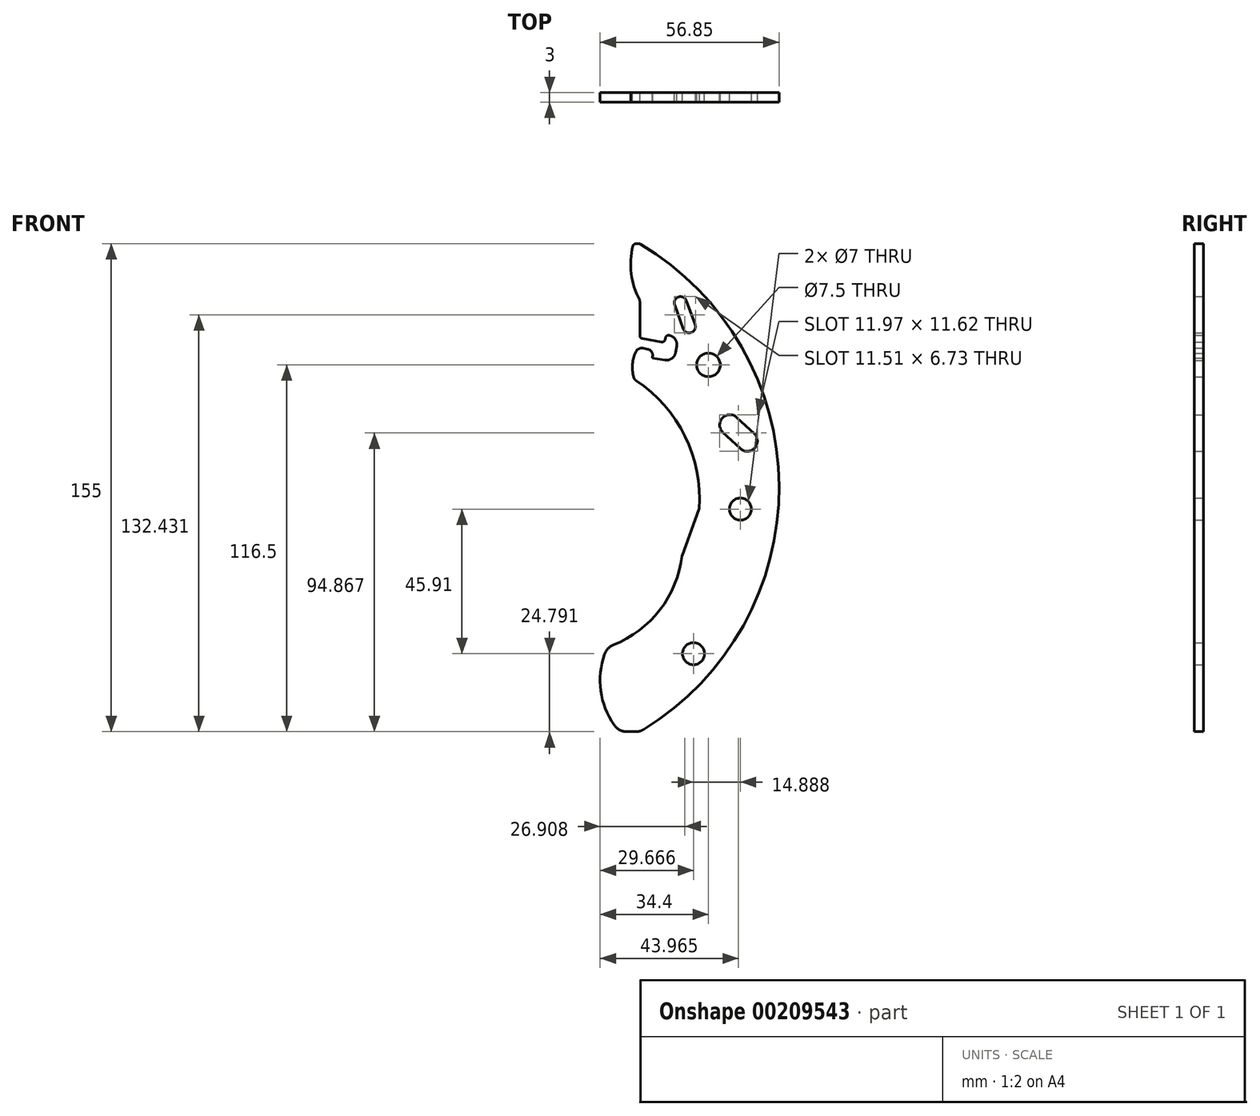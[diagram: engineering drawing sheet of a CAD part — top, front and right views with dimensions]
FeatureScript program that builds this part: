
annotation { "Feature Type Name" : "Feature", "Feature Type Description" : "" }
export const myFeature = defineFeature(function(context is Context, id is Id, definition is map)
    precondition{}
    {
        {
            var Q0;
            Q0=qCreatedBy(makeId("Front.planeOp"),FACE);
            var sketch = newSketch(context, id + "F0", { "sketchPlane" : qUnion([Q0])});
            skArc(sketch, "E0", {"start": v(46.98, -76.76) * mm, "mid": v(90, 0.58) * mm, "end": v(46, 77.36) * mm});
            skLineSegment(sketch, "E1", {"start": v(45.76, 77.5) * mm, "end": v(45.76, -77.5) * mm, "construction": true});
            skLineSegment(sketch, "E2", {"start": v(0, 0) * mm, "end": v(45.76, 0) * mm, "construction": true});
            skLineSegment(sketch, "E3", {"start": v(0, 0) * mm, "end": v(62.82, -52.7) * mm, "construction": true});
            skLineSegment(sketch, "E4", {"start": v(0, 0) * mm, "end": v(77.7, -6.8) * mm, "construction": true});
            skLineSegment(sketch, "E5", {"start": v(0, 0) * mm, "end": v(74.38, 19.93) * mm, "construction": true});
            skLineSegment(sketch, "E6", {"start": v(0, 0) * mm, "end": v(67.55, 39) * mm, "construction": true});
            skLineSegment(sketch, "E7", {"start": v(0, 0) * mm, "end": v(58.69, 58.69) * mm, "construction": true});
            skPoint(sketch, "E8", {"position": v(58.69, 58.69) * mm});
            skPoint(sketch, "E9", {"position": v(67.55, 39) * mm});
            skPoint(sketch, "E10", {"position": v(74.38, 19.93) * mm});
            skPoint(sketch, "E11", {"position": v(77.7, -6.8) * mm});
            skPoint(sketch, "E12", {"position": v(62.82, -52.7) * mm});
            skArc(sketch, "E13", {"start": v(60.57, 59.37) * mm, "mid": v(58, 60.57) * mm, "end": v(56.81, 58) * mm});
            skLineSegment(sketch, "E14", {"start": v(58.69, 58.69) * mm, "end": v(58.69, 50.69) * mm, "construction": true});
            skLineSegment(sketch, "E15", {"start": v(58.69, 58.69) * mm, "end": v(61.43, 51.17) * mm, "construction": true});
            skArc(sketch, "E16", {"start": v(59.55, 50.49) * mm, "mid": v(62.11, 49.3) * mm, "end": v(63.3, 51.86) * mm});
            skLineSegment(sketch, "E17", {"start": v(60.57, 59.37) * mm, "end": v(63.3, 51.86) * mm});
            skLineSegment(sketch, "E18", {"start": v(56.81, 58) * mm, "end": v(59.55, 50.49) * mm});
            skLineSegment(sketch, "E19", {"start": v(0, 0) * mm, "end": v(0, 89.5) * mm, "construction": true});
            skLineSegment(sketch, "E20", {"start": v(0, 89.5) * mm, "end": v(74.38, 19.93) * mm, "construction": true});
            skLineSegment(sketch, "E21", {"start": v(74.38, 19.93) * mm, "end": v(79.85, 14.8) * mm, "construction": true});
            skArc(sketch, "E22", {"start": v(76.6, 22.3) * mm, "mid": v(72, 22.15) * mm, "end": v(72.16, 17.56) * mm});
            skArc(sketch, "E23", {"start": v(77.63, 12.43) * mm, "mid": v(82.23, 12.59) * mm, "end": v(82.07, 17.18) * mm});
            skLineSegment(sketch, "E24", {"start": v(76.6, 22.3) * mm, "end": v(82.07, 17.18) * mm});
            skLineSegment(sketch, "E25", {"start": v(77.63, 12.43) * mm, "end": v(72.16, 17.56) * mm});
            skLineSegment(sketch, "E26", {"start": v(0, 0) * mm, "end": v(24.42, -17.42) * mm, "construction": true});
            skArc(sketch, "E27", {"start": v(37.4, -49.93) * mm, "mid": v(52.16, -38.77) * mm, "end": v(59.17, -21.65) * mm});
            skLineSegment(sketch, "E28", {"start": v(0, 0) * mm, "end": v(59.18, -21.54) * mm, "construction": true});
            skLineSegment(sketch, "E29", {"start": v(0, 0) * mm, "end": v(35.46, -50.64) * mm, "construction": true});
            skLineSegment(sketch, "E30", {"start": v(0, 0) * mm, "end": v(19.7, -3.47) * mm, "construction": true});
            skArc(sketch, "E31", {"start": v(45.76, -40.16) * mm, "mid": v(46.32, -39.75) * mm, "end": v(46.88, -39.34) * mm, "construction": true});
            skLineSegment(sketch, "E32", {"start": v(0, 0) * mm, "end": v(44.02, 34.39) * mm, "construction": true});
            skLineSegment(sketch, "E33", {"start": v(0, 0) * mm, "end": v(64.57, -6.79) * mm, "construction": true});
            skArc(sketch, "E34.trimOffspring", {"start": v(64.58, -6.65) * mm, "mid": v(60.09, 16.37) * mm, "end": v(44.62, 34) * mm});
            skLineSegment(sketch, "E35", {"start": v(64.53, -6.92) * mm, "end": v(59.22, -21.43) * mm});
            skLineSegment(sketch, "E36", {"start": v(44.37, -77.5) * mm, "end": v(41.7, -77.5) * mm});
            skArc(sketch, "E37", {"start": v(34.53, -52.93) * mm, "mid": v(33.38, -64.5) * mm, "end": v(37.59, -75.34) * mm});
            skPoint(sketch, "E38.visualSharp", {"position": v(35.46, -50.64) * mm});
            skArc(sketch, "E38.filletArc", {"start": v(37.4, -49.93) * mm, "mid": v(35.64, -51.12) * mm, "end": v(34.53, -52.93) * mm});
            skPoint(sketch, "E39.visualSharp", {"position": v(39.26, -77.5) * mm});
            skArc(sketch, "E39.filletArc", {"start": v(37.59, -75.34) * mm, "mid": v(39.38, -76.93) * mm, "end": v(41.7, -77.5) * mm});
            skPoint(sketch, "E40.visualSharp", {"position": v(45.76, -77.5) * mm});
            skArc(sketch, "E40.filletArc", {"start": v(44.37, -77.5) * mm, "mid": v(45.73, -77.31) * mm, "end": v(46.98, -76.76) * mm});
            skLineSegment(sketch, "E41", {"start": v(45.48, 77.5) * mm, "end": v(44.53, 77.5) * mm});
            skPoint(sketch, "E42", {"position": v(45.76, 59.5) * mm});
            skArc(sketch, "E43", {"start": v(43.56, 76.74) * mm, "mid": v(43.03, 68.04) * mm, "end": v(45.64, 59.72) * mm});
            skLineSegment(sketch, "E44", {"start": v(45.76, 59.25) * mm, "end": v(45.76, 48.34) * mm});
            skLineSegment(sketch, "E45", {"start": v(46.58, 47.35) * mm, "end": v(52.65, 46.28) * mm});
            skLineSegment(sketch, "E46", {"start": v(53.8, 47.1) * mm, "end": v(53.9, 47.59) * mm});
            skLineSegment(sketch, "E47", {"start": v(55.05, 48.4) * mm, "end": v(55.05, 48.4) * mm});
            skLineSegment(sketch, "E48", {"start": v(57.49, 44.92) * mm, "end": v(57.14, 42.95) * mm});
            skLineSegment(sketch, "E49", {"start": v(53.67, 40.52) * mm, "end": v(49.73, 41.22) * mm});
            skLineSegment(sketch, "E50", {"start": v(49.73, 41.22) * mm, "end": v(49.81, 41.7) * mm});
            skLineSegment(sketch, "E51", {"start": v(48.2, 44.02) * mm, "end": v(46.65, 44.3) * mm});
            skArc(sketch, "E52", {"start": v(44.49, 43.16) * mm, "mid": v(43.45, 39.22) * mm, "end": v(43.79, 35.16) * mm});
            skPoint(sketch, "E53.visualSharp", {"position": v(56.62, 40) * mm});
            skArc(sketch, "E53.filletArc", {"start": v(53.67, 40.52) * mm, "mid": v(55.9, 41.02) * mm, "end": v(57.14, 42.95) * mm});
            skPoint(sketch, "E54.visualSharp", {"position": v(58, 47.88) * mm});
            skArc(sketch, "E54.filletArc", {"start": v(57.49, 44.92) * mm, "mid": v(57, 47.17) * mm, "end": v(55.05, 48.4) * mm});
            skPoint(sketch, "E55.visualSharp", {"position": v(53.64, 46.11) * mm});
            skArc(sketch, "E55.filletArc", {"start": v(52.65, 46.28) * mm, "mid": v(53.4, 46.45) * mm, "end": v(53.8, 47.1) * mm});
            skPoint(sketch, "E56.visualSharp", {"position": v(54.07, 48.57) * mm});
            skArc(sketch, "E56.filletArc", {"start": v(55.05, 48.4) * mm, "mid": v(54.3, 48.23) * mm, "end": v(53.9, 47.59) * mm});
            skPoint(sketch, "E57.visualSharp", {"position": v(50.16, 43.68) * mm});
            skArc(sketch, "E57.filletArc", {"start": v(49.81, 41.7) * mm, "mid": v(49.48, 43.2) * mm, "end": v(48.2, 44.02) * mm});
            skPoint(sketch, "E58.visualSharp", {"position": v(45.24, 44.55) * mm});
            skArc(sketch, "E58.filletArc", {"start": v(46.65, 44.3) * mm, "mid": v(45.38, 44.1) * mm, "end": v(44.49, 43.16) * mm});
            skPoint(sketch, "E59.visualSharp", {"position": v(44.02, 34.39) * mm});
            skArc(sketch, "E59.filletArc", {"start": v(43.79, 35.16) * mm, "mid": v(44.1, 34.5) * mm, "end": v(44.62, 34) * mm});
            skPoint(sketch, "E60.visualSharp", {"position": v(45.76, 47.5) * mm});
            skArc(sketch, "E60.filletArc", {"start": v(45.76, 48.34) * mm, "mid": v(46, 47.7) * mm, "end": v(46.58, 47.35) * mm});
            skPoint(sketch, "E61.visualSharp", {"position": v(45.76, 77.5) * mm});
            skArc(sketch, "E61.filletArc", {"start": v(46, 77.36) * mm, "mid": v(45.75, 77.46) * mm, "end": v(45.48, 77.5) * mm});
            skPoint(sketch, "E62.visualSharp", {"position": v(43.76, 77.5) * mm});
            skArc(sketch, "E62.filletArc", {"start": v(44.53, 77.5) * mm, "mid": v(43.91, 77.29) * mm, "end": v(43.56, 76.74) * mm});
            skArc(sketch, "E63.filletArc", {"start": v(45.76, 59.25) * mm, "mid": v(45.73, 59.49) * mm, "end": v(45.64, 59.72) * mm});
            skPoint(sketch, "E64.visualSharp", {"position": v(59.18, -21.54) * mm});
            skArc(sketch, "E64.filletArc", {"start": v(59.22, -21.43) * mm, "mid": v(59.19, -21.54) * mm, "end": v(59.17, -21.65) * mm});
            skPoint(sketch, "E65.visualSharp", {"position": v(64.57, -6.79) * mm});
            skArc(sketch, "E65.filletArc", {"start": v(64.53, -6.92) * mm, "mid": v(64.56, -6.78) * mm, "end": v(64.58, -6.65) * mm});
            skSolve(sketch);
        }
        {
            var Q0;
            Q0 = qSketchRegion(id + "F0", true);
            extrude(context, id + "F1", {"entities" : qUnion([Q0]), "depth" : 3 * mm});
        }
        {
            var Q0;
            Q0=sQuery(id+"F0.wireOp",VERTEX,"E9");
            var Q1;
            Q1=makeQuery(id+"F1.opExtrude","SWEPT_BODY",BODY,{"disambiguationData":[OSD([sQuery(id+"F0.wireOp",EDGE,"E0"),sQuery(id+"F0.wireOp",EDGE,"E13"),sQuery(id+"F0.wireOp",EDGE,"E16"),sQuery(id+"F0.wireOp",EDGE,"E17"),sQuery(id+"F0.wireOp",EDGE,"E18"),sQuery(id+"F0.wireOp",EDGE,"E22"),sQuery(id+"F0.wireOp",EDGE,"E23"),sQuery(id+"F0.wireOp",EDGE,"E24"),sQuery(id+"F0.wireOp",EDGE,"E25"),sQuery(id+"F0.wireOp",EDGE,"E27"),sQuery(id+"F0.wireOp",EDGE,"E34.trimOffspring"),sQuery(id+"F0.wireOp",EDGE,"E35"),sQuery(id+"F0.wireOp",EDGE,"E36"),sQuery(id+"F0.wireOp",EDGE,"E37"),sQuery(id+"F0.wireOp",EDGE,"E38.filletArc"),sQuery(id+"F0.wireOp",EDGE,"E39.filletArc"),sQuery(id+"F0.wireOp",EDGE,"E40.filletArc"),sQuery(id+"F0.wireOp",EDGE,"E41"),sQuery(id+"F0.wireOp",EDGE,"E43"),sQuery(id+"F0.wireOp",EDGE,"E44"),sQuery(id+"F0.wireOp",EDGE,"E45"),sQuery(id+"F0.wireOp",EDGE,"E46"),sQuery(id+"F0.wireOp",EDGE,"E48"),sQuery(id+"F0.wireOp",EDGE,"E49"),sQuery(id+"F0.wireOp",EDGE,"E50"),sQuery(id+"F0.wireOp",EDGE,"E51"),sQuery(id+"F0.wireOp",EDGE,"E52"),sQuery(id+"F0.wireOp",EDGE,"E53.filletArc"),sQuery(id+"F0.wireOp",EDGE,"E54.filletArc"),sQuery(id+"F0.wireOp",EDGE,"E55.filletArc"),sQuery(id+"F0.wireOp",EDGE,"E56.filletArc"),sQuery(id+"F0.wireOp",EDGE,"E57.filletArc"),sQuery(id+"F0.wireOp",EDGE,"E58.filletArc"),sQuery(id+"F0.wireOp",EDGE,"E59.filletArc"),sQuery(id+"F0.wireOp",EDGE,"E60.filletArc"),sQuery(id+"F0.wireOp",EDGE,"E61.filletArc"),sQuery(id+"F0.wireOp",EDGE,"E62.filletArc"),sQuery(id+"F0.wireOp",EDGE,"E63.filletArc"),sQuery(id+"F0.wireOp",EDGE,"E64.filletArc"),sQuery(id+"F0.wireOp",EDGE,"E65.filletArc")])]});
            hole(context, id + "F2", {"style" : HoleStyle.SIMPLE, "endStyle" : HoleEndStyle.THROUGH, "oppositeDirection" : true, "holeDiameter" : 7.5 * mm, "locations" : qUnion([Q0]), "scope" : qUnion([Q1]), "isTappedThrough" : true});
        }
        {
            var Q0;
            Q0=sQuery(id+"F0.wireOp",VERTEX,"E11");
            var Q1;
            Q1=sQuery(id+"F0.wireOp",VERTEX,"E12");
            var Q2;
            Q2=makeQuery(id+"F1.opExtrude","SWEPT_BODY",BODY,{"disambiguationData":[OSD([sQuery(id+"F0.wireOp",EDGE,"E0"),sQuery(id+"F0.wireOp",EDGE,"E13"),sQuery(id+"F0.wireOp",EDGE,"E16"),sQuery(id+"F0.wireOp",EDGE,"E17"),sQuery(id+"F0.wireOp",EDGE,"E18"),sQuery(id+"F0.wireOp",EDGE,"E22"),sQuery(id+"F0.wireOp",EDGE,"E23"),sQuery(id+"F0.wireOp",EDGE,"E24"),sQuery(id+"F0.wireOp",EDGE,"E25"),sQuery(id+"F0.wireOp",EDGE,"E27"),sQuery(id+"F0.wireOp",EDGE,"E34.trimOffspring"),sQuery(id+"F0.wireOp",EDGE,"E35"),sQuery(id+"F0.wireOp",EDGE,"E36"),sQuery(id+"F0.wireOp",EDGE,"E37"),sQuery(id+"F0.wireOp",EDGE,"E38.filletArc"),sQuery(id+"F0.wireOp",EDGE,"E39.filletArc"),sQuery(id+"F0.wireOp",EDGE,"E40.filletArc"),sQuery(id+"F0.wireOp",EDGE,"E41"),sQuery(id+"F0.wireOp",EDGE,"E43"),sQuery(id+"F0.wireOp",EDGE,"E44"),sQuery(id+"F0.wireOp",EDGE,"E45"),sQuery(id+"F0.wireOp",EDGE,"E46"),sQuery(id+"F0.wireOp",EDGE,"E48"),sQuery(id+"F0.wireOp",EDGE,"E49"),sQuery(id+"F0.wireOp",EDGE,"E50"),sQuery(id+"F0.wireOp",EDGE,"E51"),sQuery(id+"F0.wireOp",EDGE,"E52"),sQuery(id+"F0.wireOp",EDGE,"E53.filletArc"),sQuery(id+"F0.wireOp",EDGE,"E54.filletArc"),sQuery(id+"F0.wireOp",EDGE,"E55.filletArc"),sQuery(id+"F0.wireOp",EDGE,"E56.filletArc"),sQuery(id+"F0.wireOp",EDGE,"E57.filletArc"),sQuery(id+"F0.wireOp",EDGE,"E58.filletArc"),sQuery(id+"F0.wireOp",EDGE,"E59.filletArc"),sQuery(id+"F0.wireOp",EDGE,"E60.filletArc"),sQuery(id+"F0.wireOp",EDGE,"E61.filletArc"),sQuery(id+"F0.wireOp",EDGE,"E62.filletArc"),sQuery(id+"F0.wireOp",EDGE,"E63.filletArc"),sQuery(id+"F0.wireOp",EDGE,"E64.filletArc"),sQuery(id+"F0.wireOp",EDGE,"E65.filletArc")])]});
            hole(context, id + "F3", {"style" : HoleStyle.SIMPLE, "endStyle" : HoleEndStyle.THROUGH, "oppositeDirection" : true, "holeDiameter" : 7 * mm, "locations" : qUnion([Q0, Q1]), "scope" : qUnion([Q2]), "isTappedThrough" : true});
        }
    });
